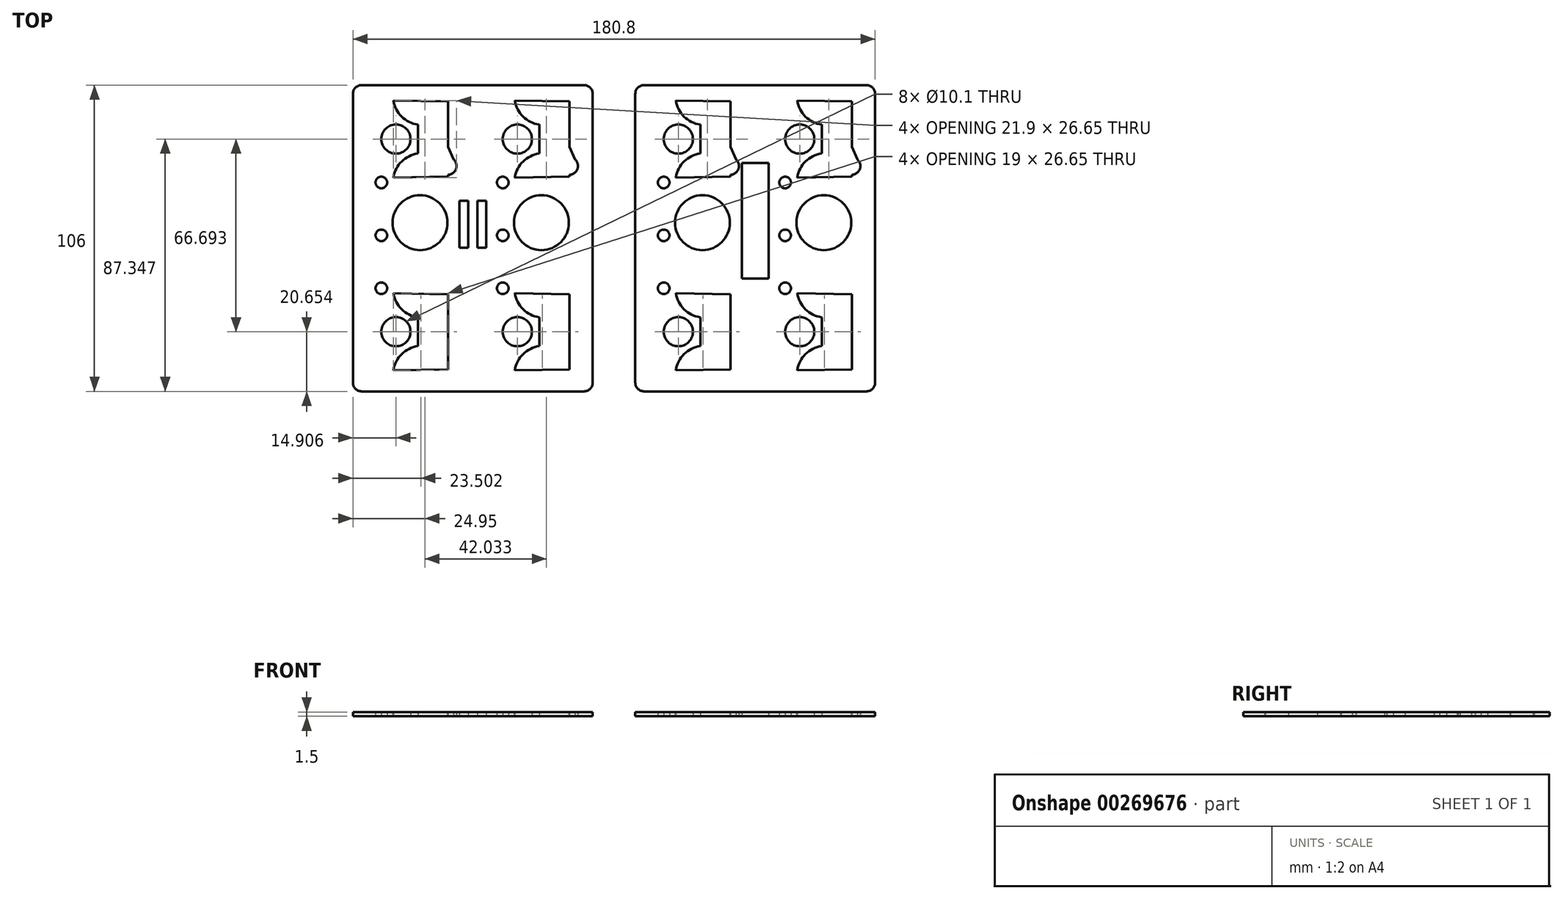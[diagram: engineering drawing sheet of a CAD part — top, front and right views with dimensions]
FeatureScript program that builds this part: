
annotation { "Feature Type Name" : "Feature", "Feature Type Description" : "" }
export const myFeature = defineFeature(function(context is Context, id is Id, definition is map)
    precondition{}
    {
        {
            var Q0;
            Q0=qCreatedBy(makeId("Top.planeOp"),FACE);
            var sketch = newSketch(context, id + "F0", { "sketchPlane" : qUnion([Q0])});
            skLineSegment(sketch, "E0.bottom", {"start": v(-14.02, 51.8) * mm, "end": v(26.98, 51.8) * mm});
            skLineSegment(sketch, "E0.top", {"start": v(-14.02, -54.2) * mm, "end": v(26.98, -54.2) * mm});
            skLineSegment(sketch, "E0.left", {"start": v(-14.02, 51.8) * mm, "end": v(-14.02, -54.2) * mm});
            skLineSegment(sketch, "E0.right", {"start": v(26.98, 51.8) * mm, "end": v(26.98, -54.2) * mm});
            skArc(sketch, "E1", {"start": v(-0.02, 46.46) * mm, "mid": v(2.88, 40.91) * mm, "end": v(8.48, 38.14) * mm});
            skLineSegment(sketch, "E2", {"start": v(8.48, 38.14) * mm, "end": v(8.48, 28.14) * mm});
            skLineSegment(sketch, "E3", {"start": v(-4.2, 33.14) * mm, "end": v(30.11, 33.14) * mm, "construction": true});
            skArc(sketch, "E4.MirrorCS", {"start": v(-0.02, 19.81) * mm, "mid": v(2.88, 25.36) * mm, "end": v(8.48, 28.14) * mm});
            skCircle(sketch, "E5", {"center": v(5.37, 41.64) * mm, "radius": 1.5 * mm});
            skCircle(sketch, "E6.MirrorC", {"center": v(5.37, 24.64) * mm, "radius": 1.5 * mm});
            skCircle(sketch, "E7", {"center": v(0.89, 33.14) * mm, "radius": 5.05 * mm});
            skLineSegment(sketch, "E8", {"start": v(-20.48, -0.2) * mm, "end": v(28.53, -0.2) * mm, "construction": true});
            skCircle(sketch, "E9.MirrorC", {"center": v(5.37, -25.06) * mm, "radius": 1.5 * mm});
            skArc(sketch, "E10.MirrorCS", {"start": v(-0.02, -20.23) * mm, "mid": v(2.88, -25.78) * mm, "end": v(8.48, -28.56) * mm});
            skLineSegment(sketch, "E11.MirrorCS", {"start": v(8.48, -38.56) * mm, "end": v(8.48, -28.56) * mm});
            skArc(sketch, "E12.MirrorCS", {"start": v(-0.02, -46.88) * mm, "mid": v(2.88, -41.33) * mm, "end": v(8.48, -38.56) * mm});
            skCircle(sketch, "E13.MirrorC", {"center": v(5.37, -42.06) * mm, "radius": 1.5 * mm});
            skCircle(sketch, "E14.MirrorC", {"center": v(0.89, -33.56) * mm, "radius": 5.05 * mm});
            skLineSegment(sketch, "E15", {"start": v(2.74, -17.29) * mm, "end": v(2.74, -48.43) * mm, "construction": true});
            skLineSegment(sketch, "E16", {"start": v(18.98, -20.6) * mm, "end": v(18.98, -46.6) * mm});
            skLineSegment(sketch, "E17", {"start": v(18.98, -46.6) * mm, "end": v(-0.02, -46.88) * mm});
            skLineSegment(sketch, "E18", {"start": v(18.98, -20.6) * mm, "end": v(-0.02, -20.23) * mm});
            skLineSegment(sketch, "E19.MirrorCS", {"start": v(18.98, 20.17) * mm, "end": v(-0.02, 19.81) * mm});
            skLineSegment(sketch, "E20.MirrorCS", {"start": v(18.98, 20.17) * mm, "end": v(18.98, 46.17) * mm});
            skLineSegment(sketch, "E21.MirrorCS", {"start": v(18.98, 46.17) * mm, "end": v(-0.02, 46.46) * mm});
            skCircle(sketch, "E22", {"center": v(9.23, 4.2) * mm, "radius": 9.5 * mm});
            skCircle(sketch, "E23", {"center": v(15.98, 29.8) * mm, "radius": 3 * mm});
            skCircle(sketch, "E24", {"center": v(18.88, 23.8) * mm, "radius": 3 * mm});
            skCircle(sketch, "E25", {"center": v(-4.17, -0.2) * mm, "radius": 2 * mm});
            skCircle(sketch, "E26", {"center": v(-4.17, -18.52) * mm, "radius": 2 * mm});
            skCircle(sketch, "E27.MirrorC", {"center": v(-4.17, 18.1) * mm, "radius": 2 * mm});
            skLineSegment(sketch, "E28", {"start": v(13.6, 27.98) * mm, "end": v(16.17, 22.51) * mm});
            skLineSegment(sketch, "E29", {"start": v(20.85, 26.06) * mm, "end": v(18.74, 30.97) * mm});
            skLineSegment(sketch, "E30.bottom", {"start": v(-56.05, 51.8) * mm, "end": v(-15.05, 51.8) * mm});
            skLineSegment(sketch, "E30.top", {"start": v(-56.05, -54.2) * mm, "end": v(-15.05, -54.2) * mm});
            skLineSegment(sketch, "E30.left", {"start": v(-56.05, 51.8) * mm, "end": v(-56.05, -54.2) * mm});
            skLineSegment(sketch, "E30.right", {"start": v(-15.05, 51.8) * mm, "end": v(-15.05, -54.2) * mm});
            skArc(sketch, "E31", {"start": v(-42.05, 46.46) * mm, "mid": v(-39.16, 40.91) * mm, "end": v(-33.55, 38.14) * mm});
            skLineSegment(sketch, "E32", {"start": v(-33.55, 38.14) * mm, "end": v(-33.55, 28.14) * mm});
            skLineSegment(sketch, "E33", {"start": v(-46.23, 33.14) * mm, "end": v(-11.92, 33.14) * mm, "construction": true});
            skArc(sketch, "E34.MirrorCS", {"start": v(-42.05, 19.81) * mm, "mid": v(-39.16, 25.36) * mm, "end": v(-33.55, 28.14) * mm});
            skCircle(sketch, "E35", {"center": v(-36.66, 41.64) * mm, "radius": 1.5 * mm});
            skCircle(sketch, "E36.MirrorC", {"center": v(-36.66, 24.64) * mm, "radius": 1.5 * mm});
            skCircle(sketch, "E37", {"center": v(-41.14, 33.14) * mm, "radius": 5.05 * mm});
            skLineSegment(sketch, "E38", {"start": v(-62.51, -0.2) * mm, "end": v(-13.5, -0.2) * mm, "construction": true});
            skCircle(sketch, "E39.MirrorC", {"center": v(-36.66, -25.06) * mm, "radius": 1.5 * mm});
            skArc(sketch, "E40.MirrorCS", {"start": v(-42.05, -20.23) * mm, "mid": v(-39.16, -25.78) * mm, "end": v(-33.55, -28.56) * mm});
            skLineSegment(sketch, "E41.MirrorCS", {"start": v(-33.55, -38.56) * mm, "end": v(-33.55, -28.56) * mm});
            skArc(sketch, "E42.MirrorCS", {"start": v(-42.05, -46.88) * mm, "mid": v(-39.16, -41.33) * mm, "end": v(-33.55, -38.56) * mm});
            skCircle(sketch, "E43.MirrorC", {"center": v(-36.66, -42.06) * mm, "radius": 1.5 * mm});
            skCircle(sketch, "E44.MirrorC", {"center": v(-41.14, -33.56) * mm, "radius": 5.05 * mm});
            skLineSegment(sketch, "E45", {"start": v(-39.3, -17.29) * mm, "end": v(-39.3, -48.43) * mm, "construction": true});
            skLineSegment(sketch, "E46", {"start": v(-23.05, -20.6) * mm, "end": v(-23.05, -46.6) * mm});
            skLineSegment(sketch, "E47", {"start": v(-23.05, -46.6) * mm, "end": v(-42.05, -46.88) * mm});
            skLineSegment(sketch, "E48", {"start": v(-23.05, -20.6) * mm, "end": v(-42.05, -20.23) * mm});
            skLineSegment(sketch, "E49.MirrorCS", {"start": v(-23.05, 20.17) * mm, "end": v(-42.05, 19.81) * mm});
            skLineSegment(sketch, "E50.MirrorCS", {"start": v(-23.05, 20.17) * mm, "end": v(-23.05, 46.17) * mm});
            skLineSegment(sketch, "E51.MirrorCS", {"start": v(-23.05, 46.17) * mm, "end": v(-42.05, 46.46) * mm});
            skCircle(sketch, "E52", {"center": v(-32.8, 4.2) * mm, "radius": 9.5 * mm});
            skCircle(sketch, "E53", {"center": v(-26.05, 29.8) * mm, "radius": 3 * mm});
            skCircle(sketch, "E54", {"center": v(-23.15, 23.8) * mm, "radius": 3 * mm});
            skCircle(sketch, "E55", {"center": v(-46.2, -0.2) * mm, "radius": 2 * mm});
            skCircle(sketch, "E56", {"center": v(-46.2, -18.52) * mm, "radius": 2 * mm});
            skCircle(sketch, "E57.MirrorC", {"center": v(-46.2, 18.1) * mm, "radius": 2 * mm});
            skLineSegment(sketch, "E58", {"start": v(-28.44, 27.98) * mm, "end": v(-25.86, 22.51) * mm});
            skLineSegment(sketch, "E59", {"start": v(-21.19, 26.06) * mm, "end": v(-23.3, 30.97) * mm});
            skLineSegment(sketch, "E60", {"start": v(-15.05, -54.2) * mm, "end": v(-14.02, -54.2) * mm});
            skLineSegment(sketch, "E61", {"start": v(-15.05, 51.8) * mm, "end": v(-14.02, 51.8) * mm});
            skLineSegment(sketch, "E62", {"start": v(-14.53, -54.2) * mm, "end": v(-14.53, 61.91) * mm, "construction": true});
            skLineSegment(sketch, "E63.bottom", {"start": v(-12.88, 11.8) * mm, "end": v(-9.88, 11.8) * mm});
            skLineSegment(sketch, "E63.top", {"start": v(-12.88, -4.5) * mm, "end": v(-9.88, -4.5) * mm});
            skLineSegment(sketch, "E63.left", {"start": v(-12.88, 11.8) * mm, "end": v(-12.88, -4.5) * mm});
            skLineSegment(sketch, "E63.right", {"start": v(-9.88, 11.8) * mm, "end": v(-9.88, -4.5) * mm});
            skLineSegment(sketch, "E64.MirrorCS", {"start": v(-16.18, 11.8) * mm, "end": v(-16.18, -4.5) * mm});
            skLineSegment(sketch, "E65.MirrorCS", {"start": v(-16.18, 11.8) * mm, "end": v(-19.18, 11.8) * mm});
            skLineSegment(sketch, "E66.MirrorCS", {"start": v(-19.18, 11.8) * mm, "end": v(-19.18, -4.5) * mm});
            skLineSegment(sketch, "E67.MirrorCS", {"start": v(-16.18, -4.5) * mm, "end": v(-19.18, -4.5) * mm});
            skLineSegment(sketch, "E68.bottom", {"start": v(83.75, 51.8) * mm, "end": v(124.75, 51.8) * mm});
            skLineSegment(sketch, "E68.top", {"start": v(83.75, -54.2) * mm, "end": v(124.75, -54.2) * mm});
            skLineSegment(sketch, "E68.left", {"start": v(83.75, 51.8) * mm, "end": v(83.75, -54.2) * mm});
            skLineSegment(sketch, "E68.right", {"start": v(124.75, 51.8) * mm, "end": v(124.75, -54.2) * mm});
            skArc(sketch, "E69", {"start": v(97.75, 46.46) * mm, "mid": v(100.64, 40.91) * mm, "end": v(106.25, 38.14) * mm});
            skLineSegment(sketch, "E70", {"start": v(106.25, 38.14) * mm, "end": v(106.25, 28.14) * mm});
            skLineSegment(sketch, "E71", {"start": v(93.57, 33.14) * mm, "end": v(127.87, 33.14) * mm, "construction": true});
            skArc(sketch, "E72.MirrorCS", {"start": v(97.75, 19.81) * mm, "mid": v(100.64, 25.36) * mm, "end": v(106.25, 28.14) * mm});
            skCircle(sketch, "E73", {"center": v(103.14, 41.64) * mm, "radius": 1.5 * mm});
            skCircle(sketch, "E74.MirrorC", {"center": v(103.14, 24.64) * mm, "radius": 1.5 * mm});
            skCircle(sketch, "E75", {"center": v(98.65, 33.14) * mm, "radius": 5.05 * mm});
            skLineSegment(sketch, "E76", {"start": v(77.28, -0.2) * mm, "end": v(126.3, -0.2) * mm, "construction": true});
            skCircle(sketch, "E77.MirrorC", {"center": v(103.14, -25.06) * mm, "radius": 1.5 * mm});
            skArc(sketch, "E78.MirrorCS", {"start": v(97.75, -20.23) * mm, "mid": v(100.64, -25.78) * mm, "end": v(106.25, -28.56) * mm});
            skLineSegment(sketch, "E79.MirrorCS", {"start": v(106.25, -38.56) * mm, "end": v(106.25, -28.56) * mm});
            skArc(sketch, "E80.MirrorCS", {"start": v(97.75, -46.88) * mm, "mid": v(100.64, -41.33) * mm, "end": v(106.25, -38.56) * mm});
            skCircle(sketch, "E81.MirrorC", {"center": v(103.14, -42.06) * mm, "radius": 1.5 * mm});
            skCircle(sketch, "E82.MirrorC", {"center": v(98.65, -33.56) * mm, "radius": 5.05 * mm});
            skLineSegment(sketch, "E83", {"start": v(100.5, -17.29) * mm, "end": v(100.5, -48.43) * mm, "construction": true});
            skLineSegment(sketch, "E84", {"start": v(116.75, -20.6) * mm, "end": v(116.75, -46.6) * mm});
            skLineSegment(sketch, "E85", {"start": v(116.75, -46.6) * mm, "end": v(97.75, -46.88) * mm});
            skLineSegment(sketch, "E86", {"start": v(116.75, -20.6) * mm, "end": v(97.75, -20.23) * mm});
            skLineSegment(sketch, "E87.MirrorCS", {"start": v(116.75, 20.17) * mm, "end": v(97.75, 19.81) * mm});
            skLineSegment(sketch, "E88.MirrorCS", {"start": v(116.75, 20.17) * mm, "end": v(116.75, 46.17) * mm});
            skLineSegment(sketch, "E89.MirrorCS", {"start": v(116.75, 46.17) * mm, "end": v(97.75, 46.46) * mm});
            skCircle(sketch, "E90", {"center": v(107, 4.2) * mm, "radius": 9.5 * mm});
            skCircle(sketch, "E91", {"center": v(113.75, 29.8) * mm, "radius": 3 * mm});
            skCircle(sketch, "E92", {"center": v(116.65, 23.8) * mm, "radius": 3 * mm});
            skCircle(sketch, "E93", {"center": v(93.6, -0.2) * mm, "radius": 2 * mm});
            skCircle(sketch, "E94", {"center": v(93.6, -18.52) * mm, "radius": 2 * mm});
            skCircle(sketch, "E95.MirrorC", {"center": v(93.6, 18.1) * mm, "radius": 2 * mm});
            skLineSegment(sketch, "E96", {"start": v(111.36, 27.98) * mm, "end": v(113.94, 22.51) * mm});
            skLineSegment(sketch, "E97", {"start": v(118.61, 26.06) * mm, "end": v(116.5, 30.97) * mm});
            skLineSegment(sketch, "E98.bottom", {"start": v(41.72, 51.8) * mm, "end": v(82.72, 51.8) * mm});
            skLineSegment(sketch, "E98.top", {"start": v(41.72, -54.2) * mm, "end": v(82.72, -54.2) * mm});
            skLineSegment(sketch, "E98.left", {"start": v(41.72, 51.8) * mm, "end": v(41.72, -54.2) * mm});
            skLineSegment(sketch, "E98.right", {"start": v(82.72, 51.8) * mm, "end": v(82.72, -54.2) * mm});
            skArc(sketch, "E99", {"start": v(55.72, 46.46) * mm, "mid": v(58.6, 40.91) * mm, "end": v(64.22, 38.14) * mm});
            skLineSegment(sketch, "E100", {"start": v(64.22, 38.14) * mm, "end": v(64.22, 28.14) * mm});
            skLineSegment(sketch, "E101", {"start": v(51.54, 33.14) * mm, "end": v(85.84, 33.14) * mm, "construction": true});
            skArc(sketch, "E102.MirrorCS", {"start": v(55.72, 19.81) * mm, "mid": v(58.6, 25.36) * mm, "end": v(64.22, 28.14) * mm});
            skCircle(sketch, "E103", {"center": v(61.1, 41.64) * mm, "radius": 1.5 * mm});
            skCircle(sketch, "E104.MirrorC", {"center": v(61.1, 24.64) * mm, "radius": 1.5 * mm});
            skCircle(sketch, "E105", {"center": v(56.62, 33.14) * mm, "radius": 5.05 * mm});
            skLineSegment(sketch, "E106", {"start": v(35.25, -0.2) * mm, "end": v(84.26, -0.2) * mm, "construction": true});
            skCircle(sketch, "E107.MirrorC", {"center": v(61.1, -25.06) * mm, "radius": 1.5 * mm});
            skArc(sketch, "E108.MirrorCS", {"start": v(55.72, -20.23) * mm, "mid": v(58.6, -25.78) * mm, "end": v(64.22, -28.56) * mm});
            skLineSegment(sketch, "E109.MirrorCS", {"start": v(64.22, -38.56) * mm, "end": v(64.22, -28.56) * mm});
            skArc(sketch, "E110.MirrorCS", {"start": v(55.72, -46.88) * mm, "mid": v(58.6, -41.33) * mm, "end": v(64.22, -38.56) * mm});
            skCircle(sketch, "E111.MirrorC", {"center": v(61.1, -42.06) * mm, "radius": 1.5 * mm});
            skCircle(sketch, "E112.MirrorC", {"center": v(56.62, -33.56) * mm, "radius": 5.05 * mm});
            skLineSegment(sketch, "E113", {"start": v(58.47, -17.29) * mm, "end": v(58.47, -48.43) * mm, "construction": true});
            skLineSegment(sketch, "E114", {"start": v(74.72, -20.6) * mm, "end": v(74.72, -46.6) * mm});
            skLineSegment(sketch, "E115", {"start": v(74.72, -46.6) * mm, "end": v(55.72, -46.88) * mm});
            skLineSegment(sketch, "E116", {"start": v(74.72, -20.6) * mm, "end": v(55.72, -20.23) * mm});
            skLineSegment(sketch, "E117.MirrorCS", {"start": v(74.72, 20.17) * mm, "end": v(55.72, 19.81) * mm});
            skLineSegment(sketch, "E118.MirrorCS", {"start": v(74.72, 20.17) * mm, "end": v(74.72, 46.17) * mm});
            skLineSegment(sketch, "E119.MirrorCS", {"start": v(74.72, 46.17) * mm, "end": v(55.72, 46.46) * mm});
            skCircle(sketch, "E120", {"center": v(64.97, 4.2) * mm, "radius": 9.5 * mm});
            skCircle(sketch, "E121", {"center": v(71.72, 29.8) * mm, "radius": 3 * mm});
            skCircle(sketch, "E122", {"center": v(74.62, 23.8) * mm, "radius": 3 * mm});
            skCircle(sketch, "E123", {"center": v(51.56, -0.2) * mm, "radius": 2 * mm});
            skCircle(sketch, "E124", {"center": v(51.56, -18.52) * mm, "radius": 2 * mm});
            skCircle(sketch, "E125.MirrorC", {"center": v(51.56, 18.1) * mm, "radius": 2 * mm});
            skLineSegment(sketch, "E126", {"start": v(69.33, 27.98) * mm, "end": v(71.9, 22.51) * mm});
            skLineSegment(sketch, "E127", {"start": v(76.58, 26.06) * mm, "end": v(74.47, 30.97) * mm});
            skLineSegment(sketch, "E128", {"start": v(82.72, -54.2) * mm, "end": v(83.75, -54.2) * mm});
            skLineSegment(sketch, "E129", {"start": v(82.72, 51.8) * mm, "end": v(83.75, 51.8) * mm});
            skLineSegment(sketch, "E130", {"start": v(83.23, -54.2) * mm, "end": v(83.23, 61.91) * mm, "construction": true});
            skLineSegment(sketch, "E131.bottom", {"start": v(84.88, 11.8) * mm, "end": v(87.88, 11.8) * mm});
            skLineSegment(sketch, "E131.top", {"start": v(84.88, -4.2) * mm, "end": v(87.88, -4.2) * mm});
            skLineSegment(sketch, "E131.left", {"start": v(84.88, 11.8) * mm, "end": v(84.88, -4.2) * mm});
            skLineSegment(sketch, "E131.right", {"start": v(87.88, 11.8) * mm, "end": v(87.88, -4.2) * mm});
            skLineSegment(sketch, "E132.MirrorCS", {"start": v(81.58, 11.8) * mm, "end": v(81.58, -4.2) * mm});
            skLineSegment(sketch, "E133.MirrorCS", {"start": v(81.58, 11.8) * mm, "end": v(78.58, 11.8) * mm});
            skLineSegment(sketch, "E134.MirrorCS", {"start": v(78.58, 11.8) * mm, "end": v(78.58, -4.2) * mm});
            skLineSegment(sketch, "E135.MirrorCS", {"start": v(81.58, -4.2) * mm, "end": v(78.58, -4.2) * mm});
            skLineSegment(sketch, "E136.bottom", {"start": v(78.58, 24.8) * mm, "end": v(87.88, 24.8) * mm});
            skLineSegment(sketch, "E136.top", {"start": v(78.58, -15.2) * mm, "end": v(87.88, -15.2) * mm});
            skLineSegment(sketch, "E136.left", {"start": v(78.58, 24.8) * mm, "end": v(78.58, -15.2) * mm});
            skLineSegment(sketch, "E136.right", {"start": v(87.88, 24.8) * mm, "end": v(87.88, -15.2) * mm});
            skSolve(sketch);
        }
        {
            var Q0;
            Q0=makeQuery(id+"F0.imprint","IMPRINT",FACE,{"disambiguationData":[TD([[makeQuery(id+"F0.imprint","IMPRINT",EDGE,{"derivedFrom":sQuery(id+"F0.wireOp",EDGE,"E30.bottom")}),-1.0]])]});
            var Q1;
            Q1=makeQuery(id+"F0.imprint","IMPRINT",FACE,{"disambiguationData":[TD([[makeQuery(id+"F0.imprint","IMPRINT",EDGE,{"derivedFrom":sQuery(id+"F0.wireOp",EDGE,"E0.left")}),-1.0]])]});
            var Q2;
            Q2=makeQuery(id+"F0.imprint","IMPRINT",FACE,{"disambiguationData":[TD([[makeQuery(id+"F0.imprint","IMPRINT",EDGE,{"derivedFrom":sQuery(id+"F0.wireOp",EDGE,"E0.bottom")}),-1.0]])]});
            var Q3;
            {var subQ9=sQuery(id+"F0.wireOp",EDGE,"E98.bottom");Q3=makeQuery(id+"F0.imprint","IMPRINT",FACE,{"disambiguationData":[TD([[makeQuery(id+"F0.imprint","IMPRINT",EDGE,{"derivedFrom":subQ9}),-1.0]])]});}
            var Q4;
            {var subQ12=sQuery(id+"F0.wireOp",EDGE,"E68.bottom");Q4=makeQuery(id+"F0.imprint","IMPRINT",FACE,{"disambiguationData":[TD([[makeQuery(id+"F0.imprint","IMPRINT",EDGE,{"derivedFrom":subQ12}),-1.0]])]});}
            var Q5;
            {var subQ0=sQuery(id+"F0.wireOp",EDGE,"E128");Q5=makeQuery(id+"F0.imprint","IMPRINT",FACE,{"disambiguationData":[TD([[makeQuery(id+"F0.imprint","IMPRINT",EDGE,{"derivedFrom":subQ0}),1.0]])]});}
            var Q6;
            {var subQ0=sQuery(id+"F0.wireOp",EDGE,"E129");Q6=makeQuery(id+"F0.imprint","IMPRINT",FACE,{"disambiguationData":[TD([[makeQuery(id+"F0.imprint","IMPRINT",EDGE,{"derivedFrom":subQ0}),-1.0]])]});}
            extrude(context, id + "F1", {"entities" : qUnion([Q0, Q1, Q2, Q3, Q4, Q5, Q6]), "depth" : 1.5 * mm});
        }
        {
            var Q0;
            Q0=makeQuery(id+"F1.opExtrude","SWEPT_EDGE",EDGE,{"disambiguationData":[OSD([sQuery(id+"F0.wireOp",EDGE,"E0.bottom"),sQuery(id+"F0.wireOp",EDGE,"E0.right")])]});
            var Q1;
            Q1=makeQuery(id+"F1.opExtrude","SWEPT_EDGE",EDGE,{"disambiguationData":[OSD([sQuery(id+"F0.wireOp",EDGE,"E98.bottom"),sQuery(id+"F0.wireOp",EDGE,"E98.left")])]});
            var Q2;
            Q2=makeQuery(id+"F1.opExtrude","SWEPT_EDGE",EDGE,{"disambiguationData":[OSD([sQuery(id+"F0.wireOp",EDGE,"E68.bottom"),sQuery(id+"F0.wireOp",EDGE,"E68.right")])]});
            var Q3;
            Q3=makeQuery(id+"F1.opExtrude","SWEPT_EDGE",EDGE,{"disambiguationData":[OSD([sQuery(id+"F0.wireOp",EDGE,"E30.bottom"),sQuery(id+"F0.wireOp",EDGE,"E30.left")])]});
            var Q4;
            Q4=makeQuery(id+"F1.opExtrude","SWEPT_EDGE",EDGE,{"disambiguationData":[OSD([sQuery(id+"F0.wireOp",EDGE,"E30.top"),sQuery(id+"F0.wireOp",EDGE,"E30.left")])]});
            var Q5;
            Q5=makeQuery(id+"F1.opExtrude","SWEPT_EDGE",EDGE,{"disambiguationData":[OSD([sQuery(id+"F0.wireOp",EDGE,"E0.top"),sQuery(id+"F0.wireOp",EDGE,"E0.right")])]});
            var Q6;
            Q6=makeQuery(id+"F1.opExtrude","SWEPT_EDGE",EDGE,{"disambiguationData":[OSD([sQuery(id+"F0.wireOp",EDGE,"E98.top"),sQuery(id+"F0.wireOp",EDGE,"E98.left")])]});
            var Q7;
            Q7=makeQuery(id+"F1.opExtrude","SWEPT_EDGE",EDGE,{"disambiguationData":[OSD([sQuery(id+"F0.wireOp",EDGE,"E68.top"),sQuery(id+"F0.wireOp",EDGE,"E68.right")])]});
            fillet(context, id + "F2", {"entities" : qUnion([Q0, Q1, Q2, Q3, Q4, Q5, Q6, Q7]), "radius" : 3 * mm, "tangentPropagation" : true, "allowEdgeOverflow" : false});
        }
    });
